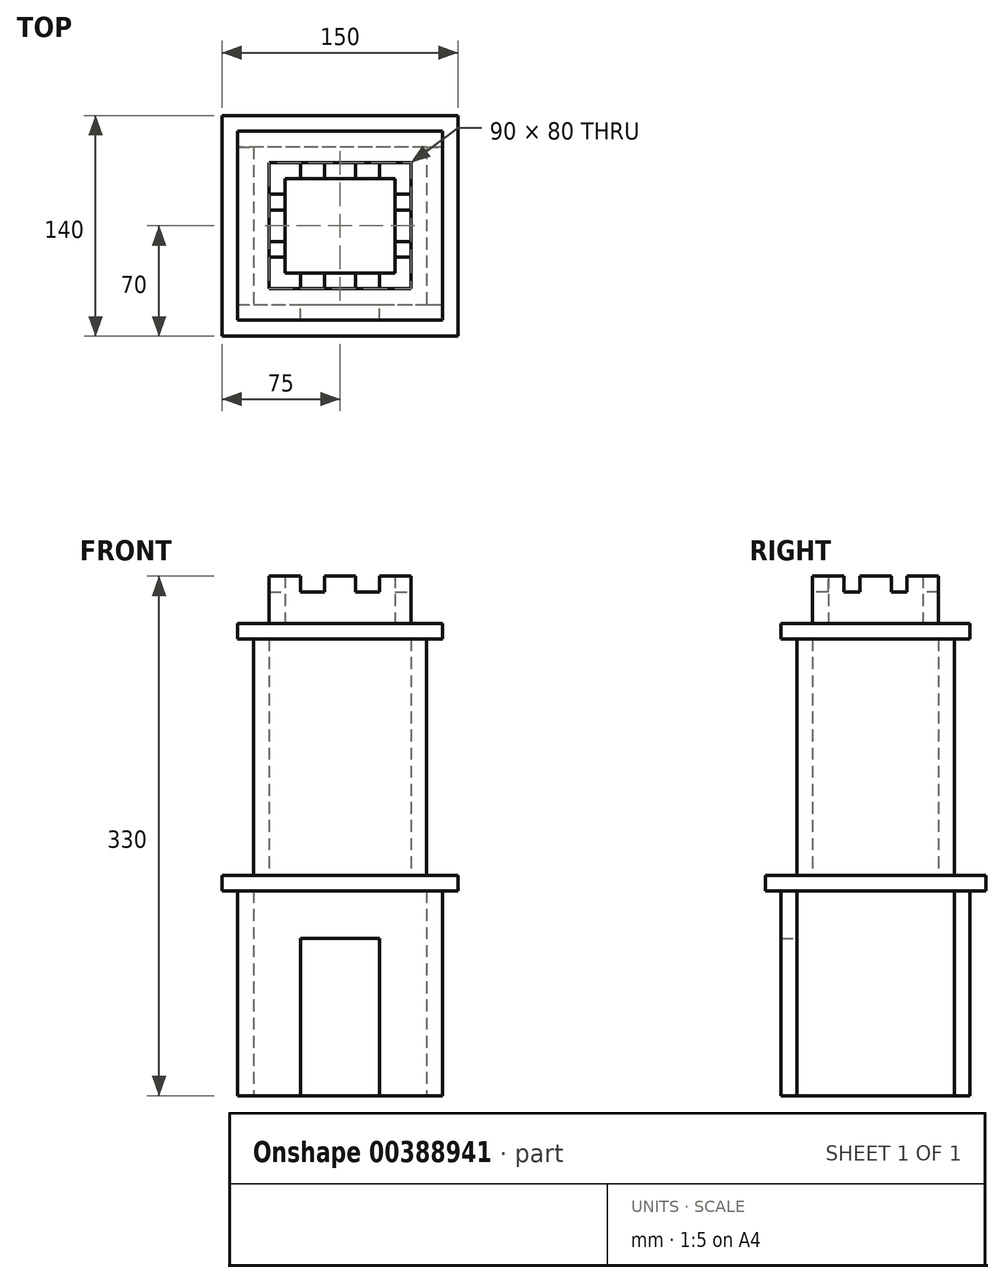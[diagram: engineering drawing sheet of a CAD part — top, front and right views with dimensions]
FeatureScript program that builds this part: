
annotation { "Feature Type Name" : "Feature", "Feature Type Description" : "" }
export const myFeature = defineFeature(function(context is Context, id is Id, definition is map)
    precondition{}
    {
        {
            var Q0;
            Q0=qCreatedBy(makeId("Front.planeOp"),FACE);
            var sketch = newSketch(context, id + "F0", { "sketchPlane" : qUnion([Q0])});
            skLineSegment(sketch, "E0.bottom", {"start": v(0, 0) * mm, "end": v(50, 0) * mm});
            skLineSegment(sketch, "E0.top", {"start": v(0, 100) * mm, "end": v(50, 100) * mm});
            skLineSegment(sketch, "E0.left", {"start": v(0, 0) * mm, "end": v(0, 100) * mm});
            skLineSegment(sketch, "E0.right", {"start": v(50, 0) * mm, "end": v(50, 100) * mm});
            skLineSegment(sketch, "E1.bottom", {"start": v(-40, 0) * mm, "end": v(90, 0) * mm});
            skLineSegment(sketch, "E1.top", {"start": v(-40, 130) * mm, "end": v(90, 130) * mm});
            skLineSegment(sketch, "E1.left", {"start": v(-40, 0) * mm, "end": v(-40, 130) * mm});
            skLineSegment(sketch, "E1.right", {"start": v(90, 0) * mm, "end": v(90, 130) * mm});
            skSolve(sketch);
        }
        {
            var Q0;
            Q0=makeQuery(id+"F0.imprint","IMPRINT",FACE,{"disambiguationData":[TD([[makeQuery(id+"F0.imprint","IMPRINT",EDGE,{"derivedFrom":sQuery(id+"F0.wireOp",EDGE,"E0.top")}),1.0]])]});
            extrude(context, id + "F1", {"entities" : qUnion([Q0]), "depth" : 10 * mm});
        }
        {
            var Q0;
            Q0=makeQuery(id+"F1.opExtrude","CAP_FACE",FACE,{"disambiguationData":[OSD([sQuery(id+"F0.wireOp",EDGE,"E0.top"),sQuery(id+"F0.wireOp",EDGE,"E0.left"),sQuery(id+"F0.wireOp",EDGE,"E0.right"),sQuery(id+"F0.wireOp",EDGE,"E1.bottom"),sQuery(id+"F0.wireOp",EDGE,"E1.top"),sQuery(id+"F0.wireOp",EDGE,"E1.left"),sQuery(id+"F0.wireOp",EDGE,"E1.right")])],"isStart":true});
            var sketch = newSketch(context, id + "F2", { "sketchPlane" : qUnion([Q0])});
            skLineSegment(sketch, "E2.bottom", {"start": v(-90, 130) * mm, "end": v(-80, 130) * mm});
            skLineSegment(sketch, "E2.top", {"start": v(-90, 0) * mm, "end": v(-80, 0) * mm});
            skLineSegment(sketch, "E2.left", {"start": v(-90, 130) * mm, "end": v(-90, 0) * mm});
            skLineSegment(sketch, "E2.right", {"start": v(-80, 130) * mm, "end": v(-80, 0) * mm});
            skLineSegment(sketch, "E3.bottom", {"start": v(40, 130) * mm, "end": v(30, 130) * mm});
            skLineSegment(sketch, "E3.top", {"start": v(40, 0) * mm, "end": v(30, 0) * mm});
            skLineSegment(sketch, "E3.left", {"start": v(40, 130) * mm, "end": v(40, 0) * mm});
            skLineSegment(sketch, "E3.right", {"start": v(30, 130) * mm, "end": v(30, 0) * mm});
            skSolve(sketch);
        }
        {
            var Q0;
            Q0 = qSketchRegion(id + "F2", true);
            extrude(context, id + "F3", {"entities" : qUnion([Q0]), "depth" : 100 * mm});
        }
        {
            var Q0;
            Q0=makeQuery(id+"F3.opExtrude","CAP_FACE",FACE,{"disambiguationData":[OSD([sQuery(id+"F2.wireOp",EDGE,"E2.bottom"),sQuery(id+"F2.wireOp",EDGE,"E2.top"),sQuery(id+"F2.wireOp",EDGE,"E2.left"),sQuery(id+"F2.wireOp",EDGE,"E2.right")])],"isStart":false});
            var sketch = newSketch(context, id + "F4", { "sketchPlane" : qUnion([Q0])});
            skLineSegment(sketch, "E4.bottom", {"start": v(-90, 130) * mm, "end": v(40, 130) * mm});
            skLineSegment(sketch, "E4.top", {"start": v(-90, 0) * mm, "end": v(40, 0) * mm});
            skLineSegment(sketch, "E4.left", {"start": v(-90, 130) * mm, "end": v(-90, 0) * mm});
            skLineSegment(sketch, "E4.right", {"start": v(40, 130) * mm, "end": v(40, 0) * mm});
            skSolve(sketch);
        }
        {
            var Q0;
            Q0 = qSketchRegion(id + "F4", true);
            extrude(context, id + "F5", {"entities" : qUnion([Q0]), "depth" : 10 * mm});
        }
        {
            var Q0;
            Q0=makeQuery(id+"F1.opExtrude","SWEPT_FACE",FACE,{"disambiguationData":[OSD([sQuery(id+"F0.wireOp",EDGE,"E1.top")])]});
            var sketch = newSketch(context, id + "F6", { "sketchPlane" : qUnion([Q0])});
            skLineSegment(sketch, "E5.0", {"start": v(-50, 120) * mm, "end": v(-50, 100) * mm});
            skLineSegment(sketch, "E5.1", {"start": v(100, 120) * mm, "end": v(-50, 120) * mm});
            skLineSegment(sketch, "E5.2", {"start": v(-50, 100) * mm, "end": v(-50, 0) * mm});
            skLineSegment(sketch, "E5.3", {"start": v(100, 120) * mm, "end": v(100, 100) * mm});
            skLineSegment(sketch, "E5.4", {"start": v(-50, -20) * mm, "end": v(-50, 0) * mm});
            skLineSegment(sketch, "E5.5", {"start": v(-50, -20) * mm, "end": v(100, -20) * mm});
            skLineSegment(sketch, "E5.6", {"start": v(100, -20) * mm, "end": v(100, 0) * mm});
            skLineSegment(sketch, "E5.7", {"start": v(100, 100) * mm, "end": v(100, 0) * mm});
            skSolve(sketch);
        }
        {
            var Q0;
            Q0 = qSketchRegion(id + "F6", true);
            extrude(context, id + "F7", {"entities" : qUnion([Q0]), "depth" : 10 * mm});
        }
        {
            var Q0;
            Q0=makeQuery(id+"F7.opExtrude","CAP_FACE",FACE,{"disambiguationData":[OSD([sQuery(id+"F6.wireOp",EDGE,"E5.0"),sQuery(id+"F6.wireOp",EDGE,"E5.1"),sQuery(id+"F6.wireOp",EDGE,"E5.2"),sQuery(id+"F6.wireOp",EDGE,"E5.3"),sQuery(id+"F6.wireOp",EDGE,"E5.4"),sQuery(id+"F6.wireOp",EDGE,"E5.5"),sQuery(id+"F6.wireOp",EDGE,"E5.6"),sQuery(id+"F6.wireOp",EDGE,"E5.7")])],"isStart":false});
            var sketch = newSketch(context, id + "F8", { "sketchPlane" : qUnion([Q0])});
            skLineSegment(sketch, "E6.0", {"start": v(-30, 100) * mm, "end": v(-30, 0) * mm});
            skLineSegment(sketch, "E6.1", {"start": v(80, 100) * mm, "end": v(-30, 100) * mm});
            skLineSegment(sketch, "E6.2", {"start": v(80, 100) * mm, "end": v(80, 0) * mm});
            skLineSegment(sketch, "E6.3", {"start": v(-30, 0) * mm, "end": v(80, 0) * mm});
            skLineSegment(sketch, "E7.0", {"start": v(70, 90) * mm, "end": v(-20, 90) * mm});
            skLineSegment(sketch, "E7.1", {"start": v(70, 90) * mm, "end": v(70, 10) * mm});
            skLineSegment(sketch, "E7.2", {"start": v(-20, 10) * mm, "end": v(70, 10) * mm});
            skLineSegment(sketch, "E7.3", {"start": v(-20, 90) * mm, "end": v(-20, 10) * mm});
            skSolve(sketch);
        }
        {
            var Q0;
            Q0 = qSketchRegion(id + "F8", true);
            extrude(context, id + "F9", {"entities" : qUnion([Q0]), "depth" : 150 * mm});
        }
        {
            var Q0;
            Q0=makeQuery(id+"F9.opExtrude","CAP_FACE",FACE,{"disambiguationData":[OSD([sQuery(id+"F8.wireOp",EDGE,"E6.0"),sQuery(id+"F8.wireOp",EDGE,"E6.1"),sQuery(id+"F8.wireOp",EDGE,"E6.2"),sQuery(id+"F8.wireOp",EDGE,"E6.3"),sQuery(id+"F8.wireOp",EDGE,"E7.0"),sQuery(id+"F8.wireOp",EDGE,"E7.1"),sQuery(id+"F8.wireOp",EDGE,"E7.2"),sQuery(id+"F8.wireOp",EDGE,"E7.3")])],"isStart":false});
            var sketch = newSketch(context, id + "F10", { "sketchPlane" : qUnion([Q0])});
            skLineSegment(sketch, "E8.0", {"start": v(-40, 110) * mm, "end": v(-40, -10) * mm});
            skLineSegment(sketch, "E8.1", {"start": v(90, 110) * mm, "end": v(-40, 110) * mm});
            skLineSegment(sketch, "E8.2", {"start": v(90, 110) * mm, "end": v(90, -10) * mm});
            skLineSegment(sketch, "E8.3", {"start": v(-40, -10) * mm, "end": v(90, -10) * mm});
            skSolve(sketch);
        }
        {
            var Q0;
            Q0 = qSketchRegion(id + "F10", true);
            extrude(context, id + "F11", {"entities" : qUnion([Q0]), "depth" : 10 * mm});
        }
        {
            var Q0;
            Q0=makeQuery(id+"F11.opExtrude","CAP_FACE",FACE,{"disambiguationData":[OSD([sQuery(id+"F10.wireOp",EDGE,"E8.0"),sQuery(id+"F10.wireOp",EDGE,"E8.1"),sQuery(id+"F10.wireOp",EDGE,"E8.2"),sQuery(id+"F10.wireOp",EDGE,"E8.3")])],"isStart":false});
            var sketch = newSketch(context, id + "F12", { "sketchPlane" : qUnion([Q0])});
            skLineSegment(sketch, "E9.0", {"start": v(70, 90) * mm, "end": v(-20, 90) * mm});
            skLineSegment(sketch, "E9.1", {"start": v(70, 90) * mm, "end": v(70, 10) * mm});
            skLineSegment(sketch, "E9.2", {"start": v(-20, 10) * mm, "end": v(70, 10) * mm});
            skLineSegment(sketch, "E9.3", {"start": v(-20, 90) * mm, "end": v(-20, 10) * mm});
            skLineSegment(sketch, "E10.0", {"start": v(-10, 80) * mm, "end": v(-10, 20) * mm});
            skLineSegment(sketch, "E10.1", {"start": v(60, 80) * mm, "end": v(-10, 80) * mm});
            skLineSegment(sketch, "E10.2", {"start": v(60, 80) * mm, "end": v(60, 20) * mm});
            skLineSegment(sketch, "E10.3", {"start": v(-10, 20) * mm, "end": v(60, 20) * mm});
            skSolve(sketch);
        }
        {
            var Q0;
            Q0 = qSketchRegion(id + "F12", true);
            extrude(context, id + "F13", {"entities" : qUnion([Q0]), "depth" : 30 * mm});
        }
        {
            var Q0;
            Q0=makeQuery(id+"F13.opExtrude","SWEPT_FACE",FACE,{"disambiguationData":[OSD([sQuery(id+"F12.wireOp",EDGE,"E9.2")])]});
            var sketch = newSketch(context, id + "F14", { "sketchPlane" : qUnion([Q0])});
            skLineSegment(sketch, "E11", {"start": v(0, 330) * mm, "end": v(0, 320) * mm});
            skLineSegment(sketch, "E12", {"start": v(0, 320) * mm, "end": v(15, 320) * mm});
            skLineSegment(sketch, "E13", {"start": v(15, 320) * mm, "end": v(15, 330) * mm});
            skLineSegment(sketch, "E14", {"start": v(15, 330) * mm, "end": v(0, 330) * mm});
            skLineSegment(sketch, "E15", {"start": v(35, 330) * mm, "end": v(35, 320) * mm});
            skLineSegment(sketch, "E16", {"start": v(35, 320) * mm, "end": v(50, 320) * mm});
            skLineSegment(sketch, "E17", {"start": v(50, 320) * mm, "end": v(50, 330) * mm});
            skSolve(sketch);
        }
        {
            var Q0;
            Q0 = qSketchRegion(id + "F14", true);
            var Q1;
            {var subQ0=sQuery(id+"F14.wireOp",EDGE,"E15");Q1=makeQuery(id+"F14.imprint","IMPRINT",FACE,{"disambiguationData":[TD([[makeQuery(id+"F14.imprint","IMPRINT",EDGE,{"derivedFrom":subQ0}),1.0]])]});}
            extrude(context, id + "F15", {"entities" : qUnion([Q0, Q1]), "operationType" : NewBodyOperationType.REMOVE, "endBound" : BoundingType.THROUGH_ALL, "oppositeDirection" : true, "depth" : 25 * mm});
        }
        {
            var Q0;
            Q0=makeQuery(id+"F13.opExtrude","SWEPT_FACE",FACE,{"disambiguationData":[OSD([sQuery(id+"F12.wireOp",EDGE,"E9.1")])]});
            var sketch = newSketch(context, id + "F16", { "sketchPlane" : qUnion([Q0])});
            skLineSegment(sketch, "E18.bottom", {"start": v(30, 330) * mm, "end": v(40, 330) * mm});
            skLineSegment(sketch, "E18.top", {"start": v(30, 320) * mm, "end": v(40, 320) * mm});
            skLineSegment(sketch, "E18.left", {"start": v(30, 330) * mm, "end": v(30, 320) * mm});
            skLineSegment(sketch, "E18.right", {"start": v(40, 330) * mm, "end": v(40, 320) * mm});
            skLineSegment(sketch, "E19.bottom", {"start": v(60, 330) * mm, "end": v(70, 330) * mm});
            skLineSegment(sketch, "E19.top", {"start": v(60, 320) * mm, "end": v(70, 320) * mm});
            skLineSegment(sketch, "E19.left", {"start": v(60, 330) * mm, "end": v(60, 320) * mm});
            skLineSegment(sketch, "E19.right", {"start": v(70, 330) * mm, "end": v(70, 320) * mm});
            skSolve(sketch);
        }
        {
            var Q0;
            Q0 = qSketchRegion(id + "F16", true);
            extrude(context, id + "F17", {"entities" : qUnion([Q0]), "operationType" : NewBodyOperationType.REMOVE, "endBound" : BoundingType.THROUGH_ALL, "oppositeDirection" : true, "depth" : 25 * mm});
        }
    });
